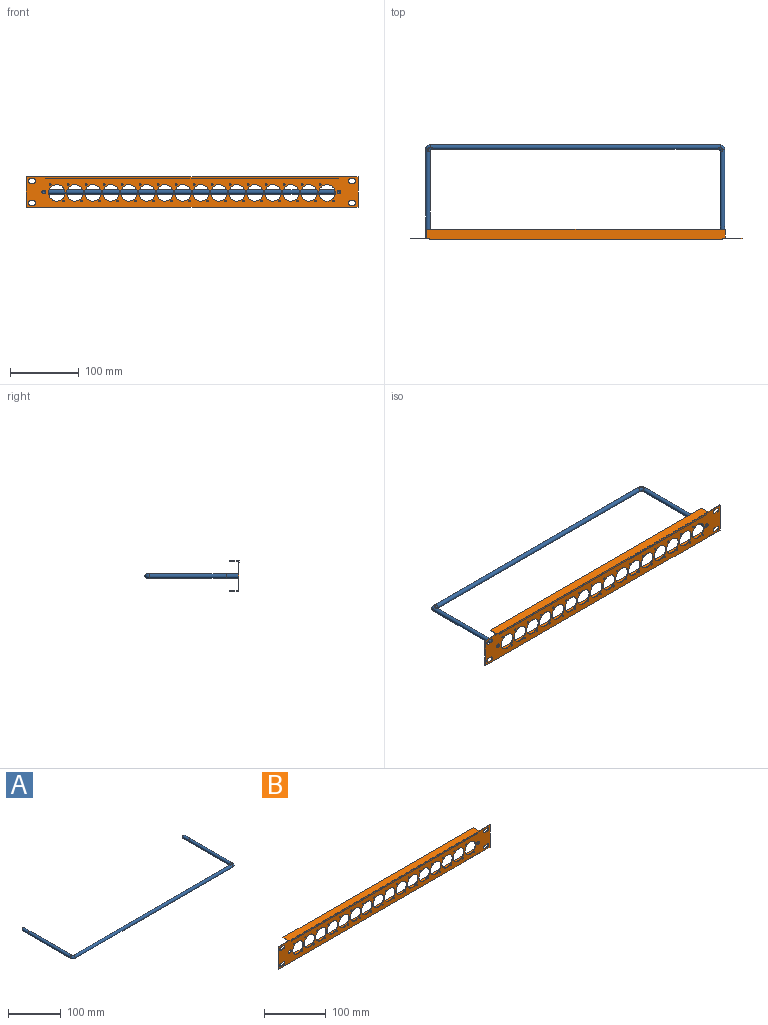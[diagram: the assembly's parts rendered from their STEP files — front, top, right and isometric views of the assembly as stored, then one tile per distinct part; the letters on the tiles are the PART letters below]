
ASSEMBLY  parts=2 mates=1
PART A: 17 faces, bbox 435.6x136.2x6.4 mm
  f0: plane 6.35x6.35mm, normal (0,0,1), area 6.5mm2, adj f12,f13,f14,f16
  f1: plane 6.35x6.35mm, normal (0,0,-1), area 6.5mm2, adj f12,f13,f14,f16
  f2: plane 6.35x6.35mm, normal (0,0,1), area 6.5mm2, adj f10,f11,f12,f15
  f3: plane 6.35x6.35mm, normal (0,0,-1), area 6.5mm2, adj f10,f11,f12,f15
  f4: plane 6.35x6.35mm, normal (0,1,0), area 11.2mm2, adj f7,f14
  f5: plane 6.35x6.35mm, normal (0,1,0), area 11.2mm2, adj f9,f10
  f6: cone r=0mm half-angle=59deg, axis (0,1,0), area 23.9mm2, adj f7
  f7: cylinder r=2.55mm len=16.51mm, axis (0,1,0), area 264.8mm2, adj f4,f6
  f8: cone r=0mm half-angle=59deg, axis (0,1,0), area 23.9mm2, adj f9
  f9: cylinder r=2.55mm len=16.51mm, axis (0,1,0), area 264.8mm2, adj f5,f8
  f10: cylinder r=3.17mm len=129.29mm, axis (0,1,0), area 2547.5mm2, adj f2,f3,f5,f11,f15
  f11: torus R=6.35mm, axis (0,0,-1), area 67.8mm2, adj f2,f3,f10,f12
  f12: cylinder r=3.17mm len=421.89mm, axis (1,0,0), area 8353.1mm2, adj f0,f1,f2,f3,f11,f13,f15,f16
  f13: torus R=6.35mm, axis (0,0,-1), area 67.8mm2, adj f0,f1,f12,f14
  f14: cylinder r=3.17mm len=129.29mm, axis (0,1,0), area 2547.5mm2, adj f0,f1,f4,f13,f16
  f15: torus R=3.17mm, axis (0,0,-1), area 81.4mm2, adj f2,f3,f10,f12
  f16: torus R=3.17mm, axis (0,0,-1), area 81.4mm2, adj f0,f1,f12,f14
PART B: 99 faces, bbox 482.6x14x44.2 mm
  f0: plane 482.6x44.2mm, normal (0,-1,0), area 12489.4mm2, adj f1,f2,f3,f4,f5,f6,f7,f8
  f1: cylinder r=12mm len=24mm, axis (0,-1,0), area 38mm2, adj f0,f15,f66
  f2: cylinder r=12mm len=24mm, axis (0,-1,0), area 38mm2, adj f0,f15,f64
  f3: cylinder r=12mm len=24mm, axis (0,-1,0), area 38mm2, adj f0,f15,f63
  f4: cylinder r=12mm len=24mm, axis (0,-1,0), area 38mm2, adj f0,f15,f62
  f5: cylinder r=12mm len=24mm, axis (0,-1,0), area 38mm2, adj f0,f15,f61
  f6: cylinder r=12mm len=24mm, axis (0,-1,0), area 38mm2, adj f0,f15,f60
  f7: cylinder r=12mm len=24mm, axis (0,-1,0), area 38mm2, adj f0,f15,f59
  f8: cylinder r=12mm len=24mm, axis (0,-1,0), area 38mm2, adj f0,f15,f58
  f9: cylinder r=12mm len=24mm, axis (0,-1,0), area 38mm2, adj f0,f15,f57
  f10: cylinder r=12mm len=24mm, axis (0,-1,0), area 38mm2, adj f0,f15,f56
  f11: cylinder r=12mm len=24mm, axis (0,-1,0), area 38mm2, adj f0,f15,f55
  f12: cylinder r=12mm len=24mm, axis (0,-1,0), area 38mm2, adj f0,f15,f54
  f13: cylinder r=12mm len=24mm, axis (0,-1,0), area 38mm2, adj f0,f15,f53
  f14: cylinder r=12mm len=24mm, axis (0,-1,0), area 38mm2, adj f0,f15,f52
  f15: plane 482.6x44.2mm, normal (0,1,0), area 12700.2mm2, adj f1,f2,f3,f4,f5,f6,f7,f8
  f16: plane 44.2x1mm, normal (-1,0,0), area 44.2mm2, adj f0,f15,f17,f19
  f17: plane 482.6x13.7mm, normal (0,0,-1), area 6001.9mm2, adj f0,f15,f16,f18,f24,f26,f27
  f18: plane 44.2x1mm, normal (1,0,0), area 44.2mm2, adj f0,f15,f17,f19
  f19: plane 482.6x13.95mm, normal (0,0,1), area 6109.9mm2, adj f0,f15,f16,f18,f20,f21,f23,f46
  f20: plane 12.7x1mm, normal (-1,0,0), area 12.7mm2, adj f15,f19,f22,f23
  f21: plane 12.7x1mm, normal (1,0,0), area 12.7mm2, adj f15,f19,f22,f23
  f22: plane 434.59x12.7mm, normal (0,0,-1), area 5519.3mm2, adj f15,f20,f21,f23
  f23: plane 434.59x1mm, normal (0,1,0), area 434.6mm2, adj f19,f20,f21,f22
  f24: plane 12.7x1mm, normal (-1,0,0), area 12.7mm2, adj f15,f17,f25,f27
  f25: plane 434.59x12.7mm, normal (0,0,1), area 5519.3mm2, adj f15,f24,f26,f27
  f26: plane 12.7x1mm, normal (1,0,0), area 12.7mm2, adj f15,f17,f25,f27
  f27: plane 434.59x1mm, normal (0,1,0), area 434.6mm2, adj f17,f24,f25,f26
  f28: plane 4.83x1mm, normal (0,0,-1), area 4.8mm2, adj f0,f15,f29,f31
  f29: cylinder r=3.17mm len=6.35mm, axis (0,-1,0), area 10mm2, adj f0,f15,f28,f30
  f30: plane 4.83x1mm, normal (0,0,1), area 4.8mm2, adj f0,f15,f29,f31
  f31: cylinder r=3.17mm len=6.35mm, axis (0,-1,0), area 10mm2, adj f0,f15,f28,f30
  f32: plane 4.83x1mm, normal (0,0,-1), area 4.8mm2, adj f0,f15,f33,f35
  f33: cylinder r=3.17mm len=6.35mm, axis (0,-1,0), area 10mm2, adj f0,f15,f32,f34
  f34: plane 4.83x1mm, normal (0,0,1), area 4.8mm2, adj f0,f15,f33,f35
  f35: cylinder r=3.17mm len=6.35mm, axis (0,-1,0), area 10mm2, adj f0,f15,f32,f34
  f36: plane 4.83x1mm, normal (0,0,-1), area 4.8mm2, adj f0,f15,f37,f39
  f37: cylinder r=3.17mm len=6.35mm, axis (0,-1,0), area 10mm2, adj f0,f15,f36,f38
  f38: plane 4.83x1mm, normal (0,0,1), area 4.8mm2, adj f0,f15,f37,f39
  f39: cylinder r=3.17mm len=6.35mm, axis (0,-1,0), area 10mm2, adj f0,f15,f36,f38
  f40: plane 4.83x1mm, normal (0,0,-1), area 4.8mm2, adj f0,f15,f41,f43
  f41: cylinder r=3.17mm len=6.35mm, axis (0,-1,0), area 10mm2, adj f0,f15,f40,f42
  f42: plane 4.83x1mm, normal (0,0,1), area 4.8mm2, adj f0,f15,f41,f43
  f43: cylinder r=3.17mm len=6.35mm, axis (0,-1,0), area 10mm2, adj f0,f15,f40,f42
  f44: cylinder r=2.79mm len=5.59mm, axis (0,-1,0), area 17.6mm2, adj f0,f15
  f45: cylinder r=2.79mm len=5.59mm, axis (0,-1,0), area 17.6mm2, adj f0,f15
  f46: plane 2.54x0.25mm, normal (1,0,0), area 0.6mm2, adj f0,f19,f49,f50
  f47: plane 1.78x0.25mm, normal (-1,0,0), area 0.5mm2, adj f0,f19,f48,f50
  f48: plane 0.76x0.25mm, normal (-1,0,-0.01), area 0.2mm2, adj f0,f47,f49,f50
  f49: plane 425.19x0.25mm, normal (0,0,-1), area 108mm2, adj f0,f46,f48,f50
  f50: plane 425.2x2.54mm, normal (0,-1,0), area 1080mm2, adj f19,f46,f47,f48,f49
  f51: cylinder r=12mm len=24mm, axis (0,-1,0), area 75.4mm2, adj f0,f15
  f52: cylinder r=12mm len=24mm, axis (0,-1,0), area 38mm2, adj f0,f14,f15
  f53: cylinder r=12mm len=24mm, axis (0,-1,0), area 38mm2, adj f0,f13,f15
  f54: cylinder r=12mm len=24mm, axis (0,-1,0), area 38mm2, adj f0,f12,f15
  f55: cylinder r=12mm len=24mm, axis (0,-1,0), area 38mm2, adj f0,f11,f15
  f56: cylinder r=12mm len=24mm, axis (0,-1,0), area 38mm2, adj f0,f10,f15
  f57: cylinder r=12mm len=24mm, axis (0,-1,0), area 38mm2, adj f0,f9,f15
  f58: cylinder r=12mm len=24mm, axis (0,-1,0), area 38mm2, adj f0,f8,f15
  f59: cylinder r=12mm len=24mm, axis (0,-1,0), area 38mm2, adj f0,f7,f15
  f60: cylinder r=12mm len=24mm, axis (0,-1,0), area 38mm2, adj f0,f6,f15
  f61: cylinder r=12mm len=24mm, axis (0,-1,0), area 38mm2, adj f0,f5,f15
  f62: cylinder r=12mm len=24mm, axis (0,-1,0), area 38mm2, adj f0,f4,f15
  f63: cylinder r=12mm len=24mm, axis (0,-1,0), area 38mm2, adj f0,f3,f15
  f64: cylinder r=12mm len=24mm, axis (0,-1,0), area 38mm2, adj f0,f2,f15
  f65: cylinder r=12mm len=24mm, axis (0,-1,0), area 75.4mm2, adj f0,f15
  f66: cylinder r=12mm len=24mm, axis (0,-1,0), area 38mm2, adj f0,f1,f15
  f67: cylinder r=1.13mm len=2.26mm, axis (0,-1,0), area 7.1mm2, adj f0,f15
  f68: cylinder r=1.13mm len=2.26mm, axis (0,-1,0), area 7.1mm2, adj f0,f15
  f69: cylinder r=1.13mm len=2.26mm, axis (0,-1,0), area 7.1mm2, adj f0,f15
  f70: cylinder r=1.13mm len=2.26mm, axis (0,-1,0), area 7.1mm2, adj f0,f15
  f71: cylinder r=1.13mm len=2.26mm, axis (0,-1,0), area 7.1mm2, adj f0,f15
  f72: cylinder r=1.13mm len=2.26mm, axis (0,-1,0), area 7.1mm2, adj f0,f15
  f73: cylinder r=1.13mm len=2.26mm, axis (0,-1,0), area 7.1mm2, adj f0,f15
  f74: cylinder r=1.13mm len=2.26mm, axis (0,-1,0), area 7.1mm2, adj f0,f15
  f75: cylinder r=1.13mm len=2.26mm, axis (0,-1,0), area 7.1mm2, adj f0,f15
  f76: cylinder r=1.13mm len=2.26mm, axis (0,-1,0), area 7.1mm2, adj f0,f15
  f77: cylinder r=1.13mm len=2.26mm, axis (0,-1,0), area 7.1mm2, adj f0,f15
  f78: cylinder r=1.13mm len=2.26mm, axis (0,-1,0), area 7.1mm2, adj f0,f15
  f79: cylinder r=1.13mm len=2.26mm, axis (0,-1,0), area 7.1mm2, adj f0,f15
  f80: cylinder r=1.13mm len=2.26mm, axis (0,-1,0), area 7.1mm2, adj f0,f15
  f81: cylinder r=1.13mm len=2.26mm, axis (0,-1,0), area 7.1mm2, adj f0,f15
  f82: cylinder r=1.13mm len=2.26mm, axis (0,-1,0), area 7.1mm2, adj f0,f15
  f83: cylinder r=1.13mm len=2.26mm, axis (0,-1,0), area 7.1mm2, adj f0,f15
  f84: cylinder r=1.13mm len=2.26mm, axis (0,-1,0), area 7.1mm2, adj f0,f15
  f85: cylinder r=1.13mm len=2.26mm, axis (0,-1,0), area 7.1mm2, adj f0,f15
  f86: cylinder r=1.13mm len=2.26mm, axis (0,-1,0), area 7.1mm2, adj f0,f15
  f87: cylinder r=1.13mm len=2.26mm, axis (0,-1,0), area 7.1mm2, adj f0,f15
  f88: cylinder r=1.13mm len=2.26mm, axis (0,-1,0), area 7.1mm2, adj f0,f15
  f89: cylinder r=1.13mm len=2.26mm, axis (0,-1,0), area 7.1mm2, adj f0,f15
  f90: cylinder r=1.13mm len=2.26mm, axis (0,-1,0), area 7.1mm2, adj f0,f15
  f91: cylinder r=1.13mm len=2.26mm, axis (0,-1,0), area 7.1mm2, adj f0,f15
  f92: cylinder r=1.13mm len=2.26mm, axis (0,-1,0), area 7.1mm2, adj f0,f15
  f93: cylinder r=1.13mm len=2.26mm, axis (0,-1,0), area 7.1mm2, adj f0,f15
  f94: cylinder r=1.13mm len=2.26mm, axis (0,-1,0), area 7.1mm2, adj f0,f15
  f95: cylinder r=1.13mm len=2.26mm, axis (0,-1,0), area 7.1mm2, adj f0,f15
  f96: cylinder r=1.13mm len=2.26mm, axis (0,-1,0), area 7.1mm2, adj f0,f15
  f97: cylinder r=1.13mm len=2.26mm, axis (0,-1,0), area 7.1mm2, adj f0,f15
  f98: cylinder r=1.13mm len=2.26mm, axis (0,-1,0), area 7.1mm2, adj f0,f15
PLACE A rot(axis=(1,0,0),180deg) t=(-28.06,74.59,-41.68)mm
PLACE B t=(-54.07,74.59,-63.78)mm
MATE fastened A.f6 <-> B.f44  axis (0,-1,0) through (-28.06,74.59,-41.68)mm
